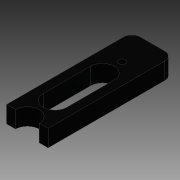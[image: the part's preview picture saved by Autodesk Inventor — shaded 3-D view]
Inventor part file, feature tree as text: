
AUTODESK INVENTOR PART (.ipt)
format: ipt  version: 2015 SP1 (Build 190203100, 203)  size: 97,792 bytes
history: native  units: in
note: dims shown in document units (in); Inventor stores cm internally (conversion verified against a paired STEP export)
features: extrude x1, sketch x1
ambient origin geometry x8: Origin, YZ Plane, XZ Plane, XY Plane, X Axis, Y Axis, Z Axis, Center Point
bodies: Solid1 (feature_tree)
feature tree (2):
  extrude  "Extrusion1"  Depth=1.225in
  sketch  "Sketch1"  dims[d0=3.7in d1=1.225in d2=0.9in d3=0.2in d4=1.4in d5=0.7in d6=0.7in d7=0.25in d8=0.5in d9=0.0in]
